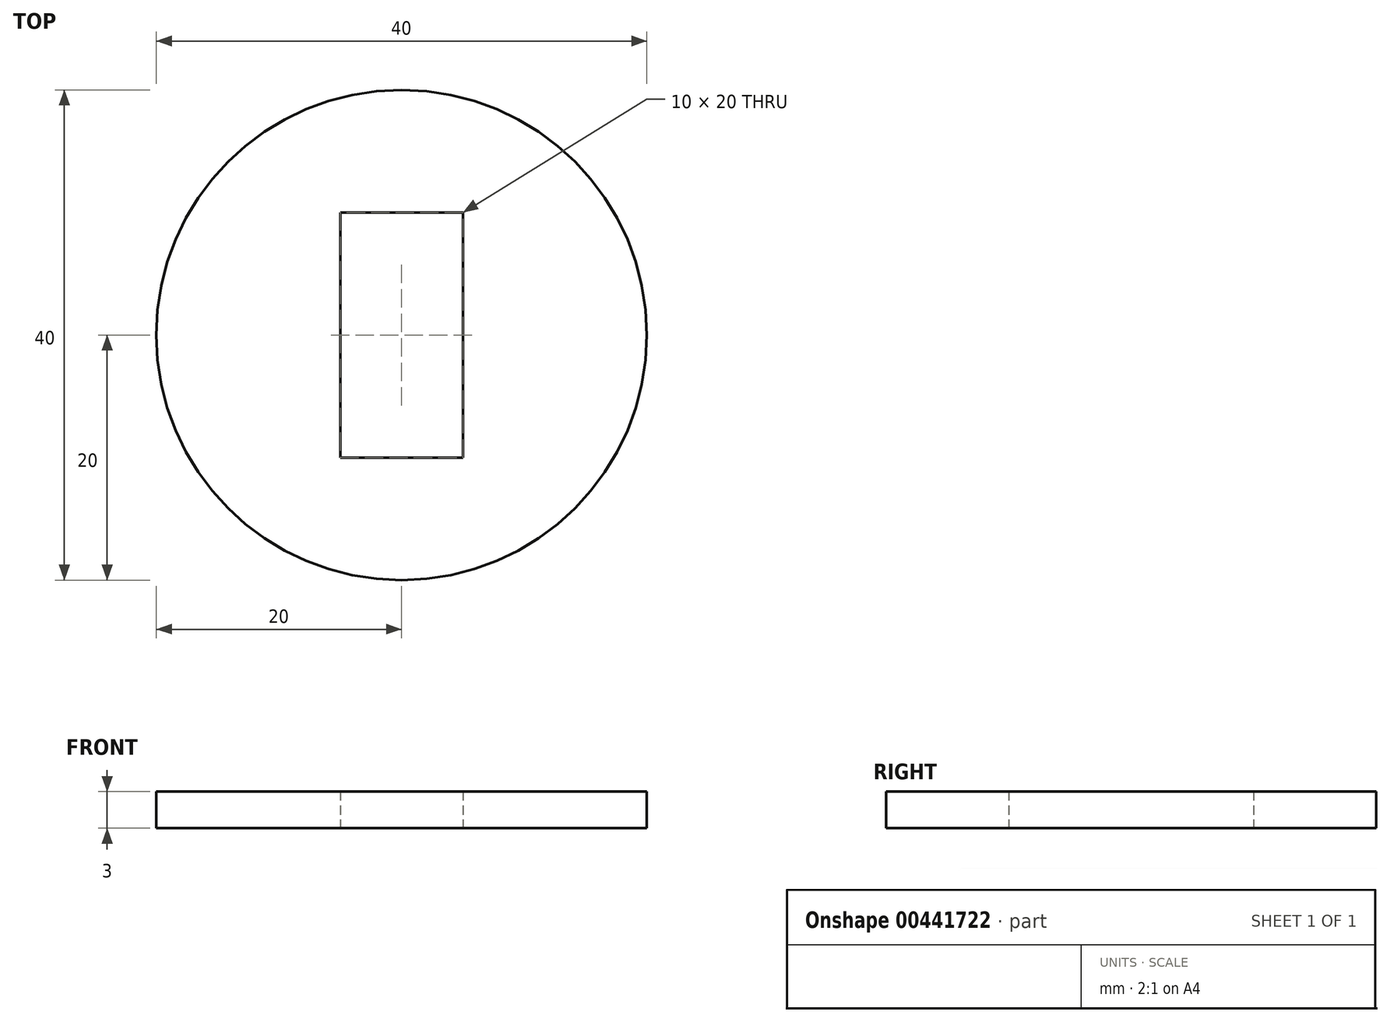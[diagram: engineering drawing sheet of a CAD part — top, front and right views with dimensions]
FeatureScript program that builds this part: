
annotation { "Feature Type Name" : "Feature", "Feature Type Description" : "" }
export const myFeature = defineFeature(function(context is Context, id is Id, definition is map)
    precondition{}
    {
        {
            var Q0;
            Q0=qCreatedBy(makeId("Top.planeOp"),FACE);
            var sketch = newSketch(context, id + "F0", { "sketchPlane" : qUnion([Q0])});
            skCircle(sketch, "E0", {"center": v(0, 0) * mm, "radius": 20 * mm});
            skLineSegment(sketch, "E1.bottom", {"start": v(-5, 10) * mm, "end": v(5, 10) * mm});
            skLineSegment(sketch, "E1.top", {"start": v(-5, -10) * mm, "end": v(5, -10) * mm});
            skLineSegment(sketch, "E1.left", {"start": v(-5, 10) * mm, "end": v(-5, -10) * mm});
            skLineSegment(sketch, "E1.right", {"start": v(5, 10) * mm, "end": v(5, -10) * mm});
            skSolve(sketch);
        }
        {
            var Q0;
            Q0 = qSketchRegion(id + "F0", true);
            extrude(context, id + "F1", {"entities" : qUnion([Q0]), "depth" : 3 * mm});
        }
    });
